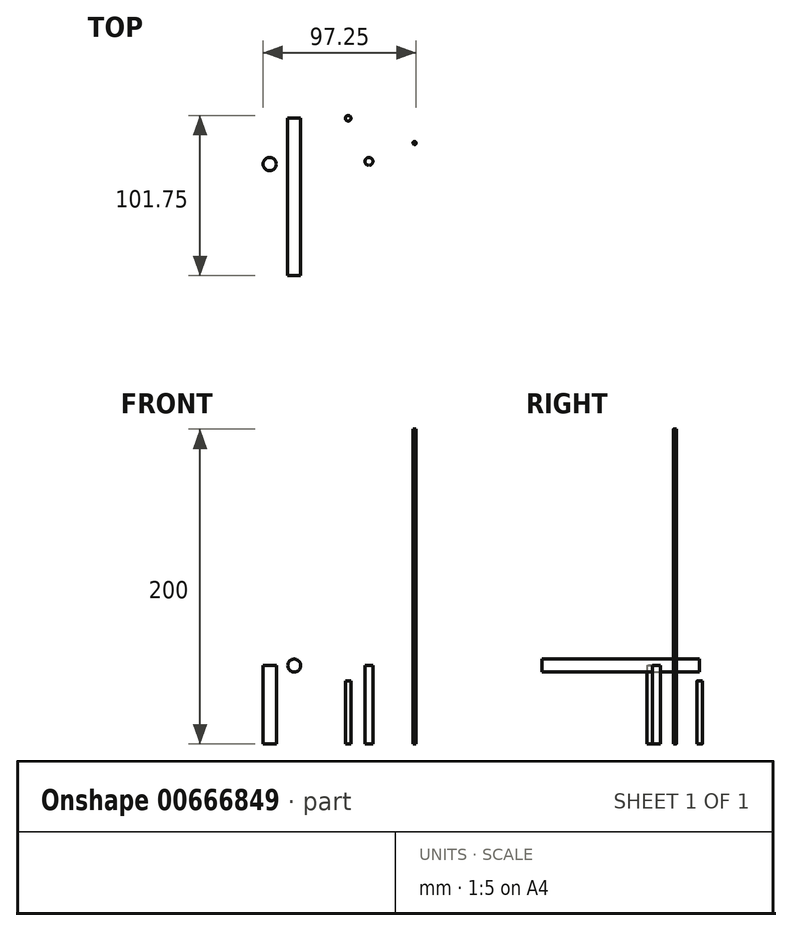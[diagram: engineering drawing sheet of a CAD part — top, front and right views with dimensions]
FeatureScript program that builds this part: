
annotation { "Feature Type Name" : "Feature", "Feature Type Description" : "" }
export const myFeature = defineFeature(function(context is Context, id is Id, definition is map)
    precondition{}
    {
        {
            var Q0;
            Q0=qCreatedBy(makeId("Top.planeOp"),FACE);
            var sketch = newSketch(context, id + "F0", { "sketchPlane" : qUnion([Q0])});
            skCircle(sketch, "E0", {"center": v(0, 0) * mm, "radius": 1.75 * mm});
            skSolve(sketch);
        }
        {
            var Q0;
            Q0 = qSketchRegion(id + "F0", true);
            extrude(context, id + "F1", {"entities" : qUnion([Q0]), "depth" : 40 * mm, "offsetDistance" : 25 * mm});
        }
        {
            var Q0;
            Q0=qCreatedBy(makeId("Top.planeOp"),FACE);
            var sketch = newSketch(context, id + "F2", { "sketchPlane" : qUnion([Q0])});
            skCircle(sketch, "E1", {"center": v(13.22, -27.4) * mm, "radius": 2.5 * mm});
            skSolve(sketch);
        }
        {
            var Q0;
            Q0=makeQuery(id+"F2.imprint","IMPRINT",FACE,{"disambiguationData":[TD([[makeQuery(id+"F2.imprint","IMPRINT",EDGE,{"derivedFrom":sQuery(id+"F2.wireOp",EDGE,"E1")}),1.0]])]});
            extrude(context, id + "F3", {"entities" : qUnion([Q0]), "depth" : 50 * mm, "offsetDistance" : 25 * mm});
        }
        {
            var Q0;
            Q0=qCreatedBy(makeId("Top.planeOp"),FACE);
            var sketch = newSketch(context, id + "F4", { "sketchPlane" : qUnion([Q0])});
            skCircle(sketch, "E2", {"center": v(-49.83, -29.1) * mm, "radius": 4.2 * mm});
            skSolve(sketch);
        }
        {
            var Q0;
            Q0 = qSketchRegion(id + "F4", true);
            extrude(context, id + "F5", {"entities" : qUnion([Q0]), "depth" : 50 * mm, "offsetDistance" : 25 * mm});
        }
        {
            var Q0;
            Q0=qCreatedBy(makeId("Top.planeOp"),FACE);
            var sketch = newSketch(context, id + "F6", { "sketchPlane" : qUnion([Q0])});
            skCircle(sketch, "E3", {"center": v(42.22, -15.74) * mm, "radius": 1 * mm});
            skSolve(sketch);
        }
        {
            var Q0;
            Q0 = qSketchRegion(id + "F6", true);
            extrude(context, id + "F7", {"entities" : qUnion([Q0]), "depth" : 200 * mm, "offsetDistance" : 25 * mm});
        }
        {
            var Q0;
            Q0=qCreatedBy(makeId("Front.planeOp"),FACE);
            var sketch = newSketch(context, id + "F8", { "sketchPlane" : qUnion([Q0])});
            skCircle(sketch, "E4", {"center": v(-34.26, 49.83) * mm, "radius": 4.1 * mm});
            skSolve(sketch);
        }
        {
            var Q0;
            Q0 = qSketchRegion(id + "F8", true);
            extrude(context, id + "F9", {"entities" : qUnion([Q0]), "depth" : 100 * mm, "offsetDistance" : 25 * mm});
        }
    });
